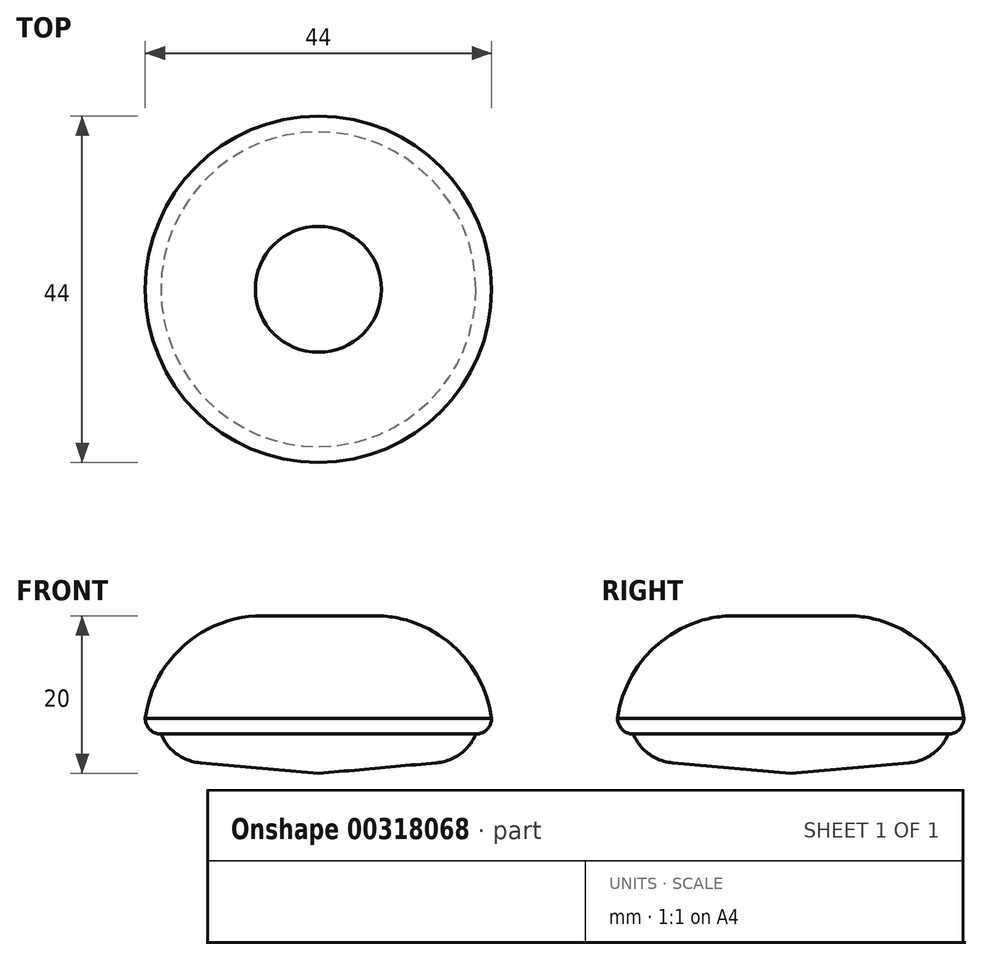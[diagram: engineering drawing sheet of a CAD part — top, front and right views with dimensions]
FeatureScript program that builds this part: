
annotation { "Feature Type Name" : "Feature", "Feature Type Description" : "" }
export const myFeature = defineFeature(function(context is Context, id is Id, definition is map)
    precondition{}
    {
        {
            var Q0;
            Q0=qCreatedBy(makeId("Front.planeOp"),FACE);
            var sketch = newSketch(context, id + "F0", { "sketchPlane" : qUnion([Q0])});
            skLineSegment(sketch, "E0", {"start": v(0, 0) * mm, "end": v(8, 0) * mm});
            skArc(sketch, "E1", {"start": v(22, -13) * mm, "mid": v(17.34, -3.98) * mm, "end": v(8, 0) * mm});
            skArc(sketch, "E2", {"start": v(20, -15) * mm, "mid": v(21.41, -14.41) * mm, "end": v(22, -13) * mm});
            skLineSegment(sketch, "E3", {"start": v(20, -15) * mm, "end": v(0, -15) * mm, "construction": true});
            skLineSegment(sketch, "E4", {"start": v(15, -18.66) * mm, "end": v(0, -20) * mm});
            skLineSegment(sketch, "E5", {"start": v(0, -20) * mm, "end": v(0, 0) * mm});
            skArc(sketch, "E6", {"start": v(15, -18.66) * mm, "mid": v(18, -17.52) * mm, "end": v(20, -15) * mm});
            skSolve(sketch);
        }
        {
            var Q0;
            Q0=makeQuery(id+"F0.imprint","IMPRINT",FACE,{"disambiguationData":[TD([[makeQuery(id+"F0.imprint","IMPRINT",EDGE,{"derivedFrom":sQuery(id+"F0.wireOp",EDGE,"E0")}),-1.0]])]});
            var Q1;
            Q1=sQuery(id+"F0.wireOp",EDGE,"E3");
            var Q2;
            Q2=sQuery(id+"F0.wireOp",EDGE,"E5");
            revolve(context, id + "F1", {"entities" : qUnion([Q0]), "surfaceEntities" : qUnion([Q1]), "axis" : qUnion([Q2]), "revolveType" : RevolveType.FULL});
        }
    });
